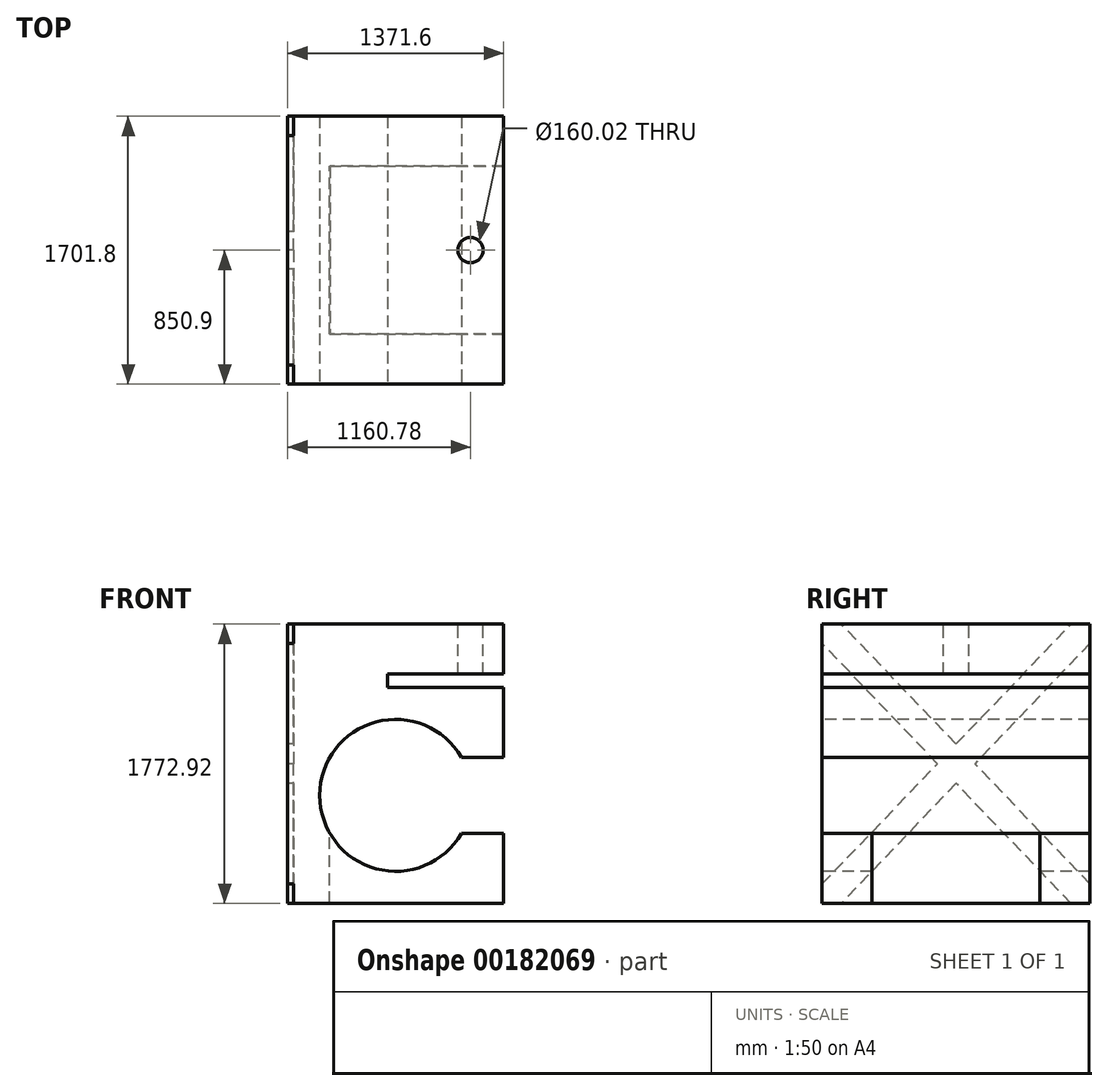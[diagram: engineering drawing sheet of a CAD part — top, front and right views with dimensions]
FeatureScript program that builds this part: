
annotation { "Feature Type Name" : "Feature", "Feature Type Description" : "" }
export const myFeature = defineFeature(function(context is Context, id is Id, definition is map)
    precondition{}
    {
        {
            var Q0;
            Q0=qCreatedBy(makeId("Front.planeOp"),FACE);
            var sketch = newSketch(context, id + "F0", { "sketchPlane" : qUnion([Q0])});
            skLineSegment(sketch, "E0", {"start": v(-47.78, -328.5) * mm, "end": v(-47.78, 1444.41) * mm});
            skLineSegment(sketch, "E1", {"start": v(-47.78, 1444.41) * mm, "end": v(1323.82, 1444.41) * mm});
            skLineSegment(sketch, "E2", {"start": v(1323.82, 1444.41) * mm, "end": v(1323.82, -328.5) * mm});
            skLineSegment(sketch, "E3", {"start": v(1323.82, -328.5) * mm, "end": v(-47.78, -328.5) * mm});
            skSolve(sketch);
        }
        {
            var Q0;
            Q0=makeQuery(id+"F0.imprint","IMPRINT",FACE,{"disambiguationData":[TD([[makeQuery(id+"F0.imprint","IMPRINT",EDGE,{"derivedFrom":sQuery(id+"F0.wireOp",EDGE,"E0")}),-1.0]])]});
            extrude(context, id + "F1", {"entities" : qUnion([Q0]), "depth" : 1701.8 * mm});
        }
        {
            var Q0;
            Q0=makeQuery(id+"F1.opExtrude","CAP_FACE",FACE,{"disambiguationData":[OSD([sQuery(id+"F0.wireOp",EDGE,"E0"),sQuery(id+"F0.wireOp",EDGE,"E1"),sQuery(id+"F0.wireOp",EDGE,"E2"),sQuery(id+"F0.wireOp",EDGE,"E3")])],"isStart":false});
            var sketch = newSketch(context, id + "F2", { "sketchPlane" : qUnion([Q0])});
            skLineSegment(sketch, "E4", {"start": v(1323.82, 1126.91) * mm, "end": v(587.22, 1126.91) * mm});
            skLineSegment(sketch, "E5", {"start": v(587.22, 1126.91) * mm, "end": v(587.22, 1043.1) * mm});
            skLineSegment(sketch, "E6", {"start": v(587.22, 1043.1) * mm, "end": v(1323.82, 1043.1) * mm});
            skLineSegment(sketch, "E7", {"start": v(1323.82, 1043.1) * mm, "end": v(1323.82, 598.6) * mm});
            skLineSegment(sketch, "E8", {"start": v(1323.82, 598.6) * mm, "end": v(1323.82, 116) * mm});
            skLineSegment(sketch, "E9", {"start": v(1323.82, 116) * mm, "end": v(1323.82, -328.5) * mm});
            skLineSegment(sketch, "E10", {"start": v(-47.78, -328.5) * mm, "end": v(638.02, -328.5) * mm});
            skLineSegment(sketch, "E11", {"start": v(638.02, -328.5) * mm, "end": v(638.02, 357.3) * mm});
            skCircle(sketch, "E12", {"center": v(638.02, 357.3) * mm, "radius": 482.6 * mm});
            skLineSegment(sketch, "E13", {"start": v(1323.82, 116) * mm, "end": v(1055.96, 116) * mm});
            skLineSegment(sketch, "E14", {"start": v(1323.82, 598.6) * mm, "end": v(1055.96, 598.6) * mm});
            skSolve(sketch);
        }
        {
            var Q0;
            {var subQ0=sQuery(id+"F2.wireOp",EDGE,"E4");Q0=makeQuery(id+"F2.imprint","IMPRINT",FACE,{"disambiguationData":[TD([[makeQuery(id+"F2.imprint","IMPRINT",EDGE,{"derivedFrom":subQ0}),1.0]])]});}
            var Q1;
            Q1=makeQuery(id+"F2.imprint","IMPRINT",FACE,{"disambiguationData":[TD([[makeQuery(id+"F2.imprint","IMPRINT",EDGE,{"derivedFrom":sQuery(id+"F2.wireOp",EDGE,"E8")}),-1.0]])]});
            var Q2;
            {var subQ0=sQuery(id+"F2.wireOp",EDGE,"E12");var subQ1=makeQuery(id+"F2.imprint","INTERSECT",VERTEX,{"derivedFrom":[subQ0,sQuery(id+"F2.wireOp",EDGE,"E14")]});Q2=makeQuery(id+"F2.imprint","IMPRINT",FACE,{"disambiguationData":[TD([[makeQuery(id+"F2.imprint","IMPRINT",EDGE,{"disambiguationData":[TD([[subQ1,-1.0]])],"derivedFrom":subQ0}),1.0]])]});}
            extrude(context, id + "F3", {"entities" : qUnion([Q0, Q1, Q2]), "operationType" : NewBodyOperationType.REMOVE, "oppositeDirection" : true, "depth" : 1701.8 * mm});
        }
        {
            var Q0;
            Q0=makeQuery(id+"F3.boolean.opBoolean","COPY",FACE,{"derivedFrom":makeQuery(id+"F3.opExtrude","SWEPT_FACE",FACE,{"disambiguationData":[OSD([sQuery(id+"F2.wireOp",EDGE,"E13")])]})});
            var sketch = newSketch(context, id + "F4", { "sketchPlane" : qUnion([Q0])});
            skLineSegment(sketch, "E15", {"start": v(1323.82, -1701.8) * mm, "end": v(1323.82, -1384.3) * mm});
            skLineSegment(sketch, "E16", {"start": v(1323.82, -1384.3) * mm, "end": v(1323.82, -317.5) * mm});
            skLineSegment(sketch, "E17", {"start": v(1323.82, -317.5) * mm, "end": v(1323.82, 0) * mm});
            skLineSegment(sketch, "E18", {"start": v(1323.82, -1384.3) * mm, "end": v(1055.96, -1384.3) * mm});
            skLineSegment(sketch, "E19", {"start": v(1323.82, -317.5) * mm, "end": v(1055.96, -317.5) * mm});
            skSolve(sketch);
        }
        {
            var Q0;
            Q0=makeQuery(id+"F4.imprint","IMPRINT",FACE,{"disambiguationData":[TD([[makeQuery(id+"F4.imprint","IMPRINT",EDGE,{"derivedFrom":sQuery(id+"F4.wireOp",EDGE,"E16")}),-1.0]])]});
            extrude(context, id + "F5", {"entities" : qUnion([Q0]), "operationType" : NewBodyOperationType.REMOVE, "oppositeDirection" : true, "depth" : 762 * mm});
        }
        {
            var Q0;
            Q0=makeQuery(id+"F5.boolean.opBoolean","COPY",FACE,{"derivedFrom":makeQuery(id+"F5.opExtrude","SWEPT_FACE",FACE,{"disambiguationData":[OSD([sQuery(id+"F2.wireOp",EDGE,"E12"),sQuery(id+"F2.wireOp",EDGE,"E13")])]})});
            extrude(context, id + "F6", {"entities" : qUnion([Q0]), "operationType" : NewBodyOperationType.REMOVE, "oppositeDirection" : true, "depth" : 838.2 * mm});
        }
        {
            var Q0;
            Q0=makeQuery(id+"F1.opExtrude","SWEPT_FACE",FACE,{"disambiguationData":[OSD([sQuery(id+"F0.wireOp",EDGE,"E1")])]});
            var sketch = newSketch(context, id + "F7", { "sketchPlane" : qUnion([Q0])});
            skLineSegment(sketch, "E20", {"start": v(1323.82, 0) * mm, "end": v(1323.82, -850.9) * mm});
            skLineSegment(sketch, "E21", {"start": v(1323.82, -850.9) * mm, "end": v(1113, -850.9) * mm});
            skCircle(sketch, "E22", {"center": v(1113, -850.9) * mm, "radius": 80.01 * mm});
            skSolve(sketch);
        }
        {
            var Q0;
            Q0=makeQuery(id+"F7.imprint","IMPRINT",FACE,{"disambiguationData":[TD([[makeQuery(id+"F7.imprint","IMPRINT",EDGE,{"derivedFrom":sQuery(id+"F7.wireOp",EDGE,"E22")}),1.0]])]});
            extrude(context, id + "F8", {"entities" : qUnion([Q0]), "operationType" : NewBodyOperationType.REMOVE, "oppositeDirection" : true, "depth" : 317.5 * mm});
        }
        {
            var Q0;
            Q0=makeQuery(id+"F1.opExtrude","SWEPT_FACE",FACE,{"disambiguationData":[OSD([sQuery(id+"F0.wireOp",EDGE,"E0")])]});
            var sketch = newSketch(context, id + "F9", { "sketchPlane" : qUnion([Q0])});
            skLineSegment(sketch, "E23", {"start": v(0, -328.5) * mm, "end": v(121.92, -328.5) * mm});
            skLineSegment(sketch, "E24", {"start": v(0, -328.5) * mm, "end": v(0, -206.59) * mm});
            skLineSegment(sketch, "E25", {"start": v(0, -206.59) * mm, "end": v(121.92, -328.5) * mm});
            skLineSegment(sketch, "E26", {"start": v(1701.8, -328.5) * mm, "end": v(1579.88, -328.5) * mm});
            skLineSegment(sketch, "E27", {"start": v(1701.8, -328.5) * mm, "end": v(1701.8, -206.59) * mm});
            skLineSegment(sketch, "E28", {"start": v(1701.8, -206.59) * mm, "end": v(1579.88, -328.5) * mm});
            skLineSegment(sketch, "E29", {"start": v(0, 1444.41) * mm, "end": v(0, 1322.5) * mm});
            skLineSegment(sketch, "E30", {"start": v(0, 1444.41) * mm, "end": v(121.92, 1444.41) * mm});
            skLineSegment(sketch, "E31", {"start": v(121.92, 1444.41) * mm, "end": v(0, 1322.5) * mm});
            skLineSegment(sketch, "E32", {"start": v(1701.8, 1444.41) * mm, "end": v(1579.88, 1444.41) * mm});
            skLineSegment(sketch, "E33", {"start": v(1701.8, 1444.41) * mm, "end": v(1701.8, 1322.5) * mm});
            skLineSegment(sketch, "E34", {"start": v(1701.8, 1322.5) * mm, "end": v(1579.88, 1444.41) * mm});
            skLineSegment(sketch, "E35", {"start": v(0, -206.59) * mm, "end": v(1579.88, 1444.41) * mm});
            skLineSegment(sketch, "E36", {"start": v(121.92, -328.5) * mm, "end": v(1701.8, 1322.5) * mm});
            skLineSegment(sketch, "E37", {"start": v(0, 1322.5) * mm, "end": v(1579.88, -328.5) * mm});
            skLineSegment(sketch, "E38", {"start": v(1701.8, -206.59) * mm, "end": v(121.92, 1444.41) * mm});
            skSolve(sketch);
        }
        {
            var Q0;
            Q0=makeQuery(id+"F9.imprint","IMPRINT",FACE,{"disambiguationData":[TD([[makeQuery(id+"F9.imprint","IMPRINT",EDGE,{"derivedFrom":sQuery(id+"F9.wireOp",EDGE,"E29")}),-1.0]])]});
            var Q1;
            Q1=makeQuery(id+"F9.imprint","IMPRINT",FACE,{"disambiguationData":[TD([[makeQuery(id+"F9.imprint","IMPRINT",EDGE,{"derivedFrom":sQuery(id+"F9.wireOp",EDGE,"E23")}),-1.0]])]});
            var Q2;
            Q2=makeQuery(id+"F9.imprint","IMPRINT",FACE,{"disambiguationData":[TD([[makeQuery(id+"F9.imprint","IMPRINT",EDGE,{"derivedFrom":sQuery(id+"F9.wireOp",EDGE,"E26")}),-1.0]])]});
            var Q3;
            Q3=makeQuery(id+"F9.imprint","IMPRINT",FACE,{"disambiguationData":[TD([[makeQuery(id+"F9.imprint","IMPRINT",EDGE,{"derivedFrom":sQuery(id+"F9.wireOp",EDGE,"E32")}),1.0]])]});
            extrude(context, id + "F10", {"entities" : qUnion([Q0, Q1, Q2, Q3]), "operationType" : NewBodyOperationType.REMOVE, "oppositeDirection" : true, "depth" : 38.1 * mm});
        }
        {
            var Q0;
            {var subQ0=sQuery(id+"F9.wireOp",EDGE,"E31");Q0=makeQuery(id+"F9.imprint","IMPRINT",FACE,{"disambiguationData":[TD([[makeQuery(id+"F9.imprint","IMPRINT",EDGE,{"derivedFrom":subQ0}),1.0]])]});}
            var Q1;
            {var subQ0=sQuery(id+"F9.wireOp",EDGE,"E37");var subQ1=sQuery(id+"F9.wireOp",EDGE,"E35");var subQ2=makeQuery(id+"F9.imprint","INTERSECT",VERTEX,{"derivedFrom":[subQ1,subQ0]});Q1=makeQuery(id+"F9.imprint","IMPRINT",FACE,{"disambiguationData":[TD([[makeQuery(id+"F9.imprint","IMPRINT",EDGE,{"disambiguationData":[TD([[subQ2,-1.0]])],"derivedFrom":subQ1}),-1.0]])]});}
            var Q2;
            {var subQ0=sQuery(id+"F9.wireOp",EDGE,"E34");Q2=makeQuery(id+"F9.imprint","IMPRINT",FACE,{"disambiguationData":[TD([[makeQuery(id+"F9.imprint","IMPRINT",EDGE,{"derivedFrom":subQ0}),1.0]])]});}
            var Q3;
            {var subQ0=sQuery(id+"F9.wireOp",EDGE,"E28");Q3=makeQuery(id+"F9.imprint","IMPRINT",FACE,{"disambiguationData":[TD([[makeQuery(id+"F9.imprint","IMPRINT",EDGE,{"derivedFrom":subQ0}),-1.0]])]});}
            var Q4;
            {var subQ0=sQuery(id+"F9.wireOp",EDGE,"E25");Q4=makeQuery(id+"F9.imprint","IMPRINT",FACE,{"disambiguationData":[TD([[makeQuery(id+"F9.imprint","IMPRINT",EDGE,{"derivedFrom":subQ0}),1.0]])]});}
            extrude(context, id + "F11", {"entities" : qUnion([Q0, Q1, Q2, Q3, Q4]), "operationType" : NewBodyOperationType.REMOVE, "oppositeDirection" : true, "depth" : 38.1 * mm});
        }
    });
